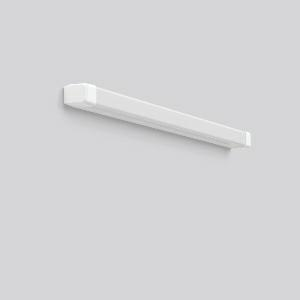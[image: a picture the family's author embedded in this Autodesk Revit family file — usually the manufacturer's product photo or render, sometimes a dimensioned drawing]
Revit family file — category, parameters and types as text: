
# Revit family: baleva_451202_002_2_452b
name_source: partatom
category: Lighting Fixtures
units: mm (PartAtom-declared; Revit-internal decimal feet)

## family parameters
Cut with Voids When Loaded = No
Host = Face
Light Source = No
Part Type = Normal
Room Calculation Point = No
Round Connector Dimension = Use Diameter
Shared = No

## types (1)
- MultiColor 830 (1 x LED Modul 830, 1550 lm, 3000)
    Apparent Load = 15 VA
    CIE Flux Codes = 40 69 89 82 100
    Color Rendering = 80
    Color Temperature = 3000
    Default Elevation = 1800 mm
    Description = Series: BALEVA
Linear luminaire with timeless functional design. Ideal for sanitary areas, corridors, waiting areas, nursing homes, patient rooms. Body and end caps made of white plastic. Diffuser made of plastic (polycarbonate), opal, shockproof. Homogeneous and smooth light distribution. MultiColour: With rear switching element, variable colour temperature 3000  K or 4000  K. Factory setting is 4000 K. Diffuser can be assembled without the use of tools. Quick and easy to install. Can be installed horizontally and vertically. 2 central cable inlets for looping the cable. Converter integrated and encapsulated. 
Colour: white
Length: 900 mm
Width: 46 mm
Height: 60 mm
Lamp: LED
Socket: without socket
Colour temperature: 3000K, 4000K
Colour rendering index (CRI): 80
System power: 15 W
Rated luminous flux: 1550 lm
Luminous efficiency: 103 lm/W
System power 2: 15 W
Rated luminous flux 2: 1650 lm
Luminous efficiency 2: 110 lm/W
Control gear: Regulated power supply
Protection class: II
Type of protection: IP 40
    Height = 60 mm  [stored 0.19685 ft]
    Lamp = 1 x LED Modul 830
    Lamp Light Flux = 1550 lm
    Lamp count = 1
    Length = 900 mm
    Lifetime = 50000 h
    Luminous efficacy = 103 lm/W
    Manufacturer = RZB
    ModVariant = No
    Model = 451202.002.2
    Mounting Place = Ceiling, Wall
    Mounting Type = Surface mounted
    Number of Poles = 1
    OnlyDefault = Yes
    Power Factor = 1
    Product Name = BALEVA
    Product group = Surface mounted ceiling and wall luminaires
    ProductGroupID = 305
    Protection Class = Protection class II
    Protection Degree = IP 40
    RLX_Detail_Level = 1
    RLX_Emergency_Light_Flux = 0 lm
    RLX_Emergency_Type = 0
    RLX_Emergency_Type_DB = No
    RlxData = <blob elided: 40237 chars, md5=b798249a>
    Socket = socket
    Standby Power = 0 W
    System Light Flux = 1550 lm
    System Power = 15 W
    Type Comments = MultiColor 830
    Type Image = 451202.002.jpg
    URL = http://relux.com
    VarID = multicolor_830
    Voltage = 230 V
    Voltage Range = 220-240 V
    Weight = 0.00 kg
    Width = 46 mm

note: [stored X ft] marks values corroborated as IEEE doubles in the binary element streams (Revit-internal decimal feet)

## geometry (parser evidence)
native form markers: Blend x4, Sweep x11
no freeform markers — native parametric forms only
